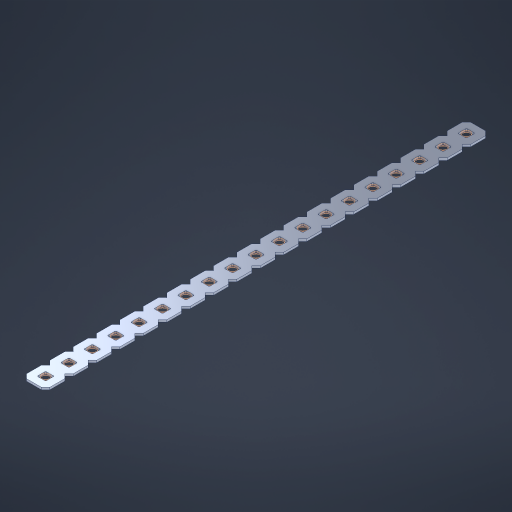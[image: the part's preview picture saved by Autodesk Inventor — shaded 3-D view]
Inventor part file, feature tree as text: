
AUTODESK INVENTOR PART (.ipt)
format: ipt  version: 2023 (Build 270158000, 158)  size: 504,832 bytes
history: native  units: in
note: dims shown in document units (in); Inventor stores cm internally (conversion verified against a paired STEP export)
features: other x20, extrude x18, sketch x2, pattern_linear x1
ambient origin geometry x8: Origin, YZ Plane, XZ Plane, XY Plane, X Axis, Y Axis, Z Axis, Center Point
bodies: Solid1 (feature_tree), Body (feature_tree)
feature tree (41):
  pattern_linear  "Rectangular Pattern1"  Spacing1=0.09in  [1 undecoded]
  sketch  "Sketch1"  dims[d1=0.5in]
  sketch  "Sketch2"  dims[d2=0.182in d3=0.09in d4=0.09in d5=0.09in d6=0.09in d7=0.09in d8=0.09in d9=0.09in d10=0.09in d11=0.02in d13=0.0in d14=0.172in d15=0.0625in d16=0.0in d19=0.5in d22=0.5in]
  other  "Srf1"
  other  "Srf126"
  other  "Srf127"
  other  "Srf128"
  other  "Srf129"
  other  "Srf130"
  other  "Srf131"
  other  "Srf250"
  other  "Srf251"
  other  "Srf252"
  other  "Srf253"
  other  "Srf254"
  other  "Srf255"
  other  "Srf256"
  other  "Srf257"
  other  "Srf258"
  other  "Srf259"
  other  "Srf260"
  other  "Srf261"
  other  "Circle"
  extrude  "ExtrusionSrf126"  Depth=0.09in
  extrude  "ExtrusionSrf127"  Depth=0.09in
  extrude  "ExtrusionSrf128"  Depth=0.09in
  extrude  "ExtrusionSrf129"  Depth=0.09in
  extrude  "ExtrusionSrf130"  Depth=0.09in
  extrude  "ExtrusionSrf131"  Depth=0.09in
  extrude  "ExtrusionSrf250"  Depth=0.09in
  extrude  "ExtrusionSrf251"  Depth=0.02in
  extrude  "ExtrusionSrf252"  TaperAngle=0.0deg  [1 undecoded]
  extrude  "ExtrusionSrf253"  Depth=0.5in
  extrude  "ExtrusionSrf254"  Depth=0.5in TaperAngle=0.0deg
  extrude  "ExtrusionSrf255"  Depth=0.5in
  extrude  "ExtrusionSrf256"  Depth=0.5in
  extrude  "ExtrusionSrf257"  [1 undecoded]
  extrude  "ExtrusionSrf258"  [1 undecoded]
  extrude  "ExtrusionSrf259"  [1 undecoded]
  extrude  "ExtrusionSrf260"  [1 undecoded]
  extrude  "ExtrusionSrf261"  [1 undecoded]
note: 7 required parameter values undecoded (feature->parameter linkage not recoverable at this tier; creation-order binding heuristic only, values carry confidence <= 0.55)
